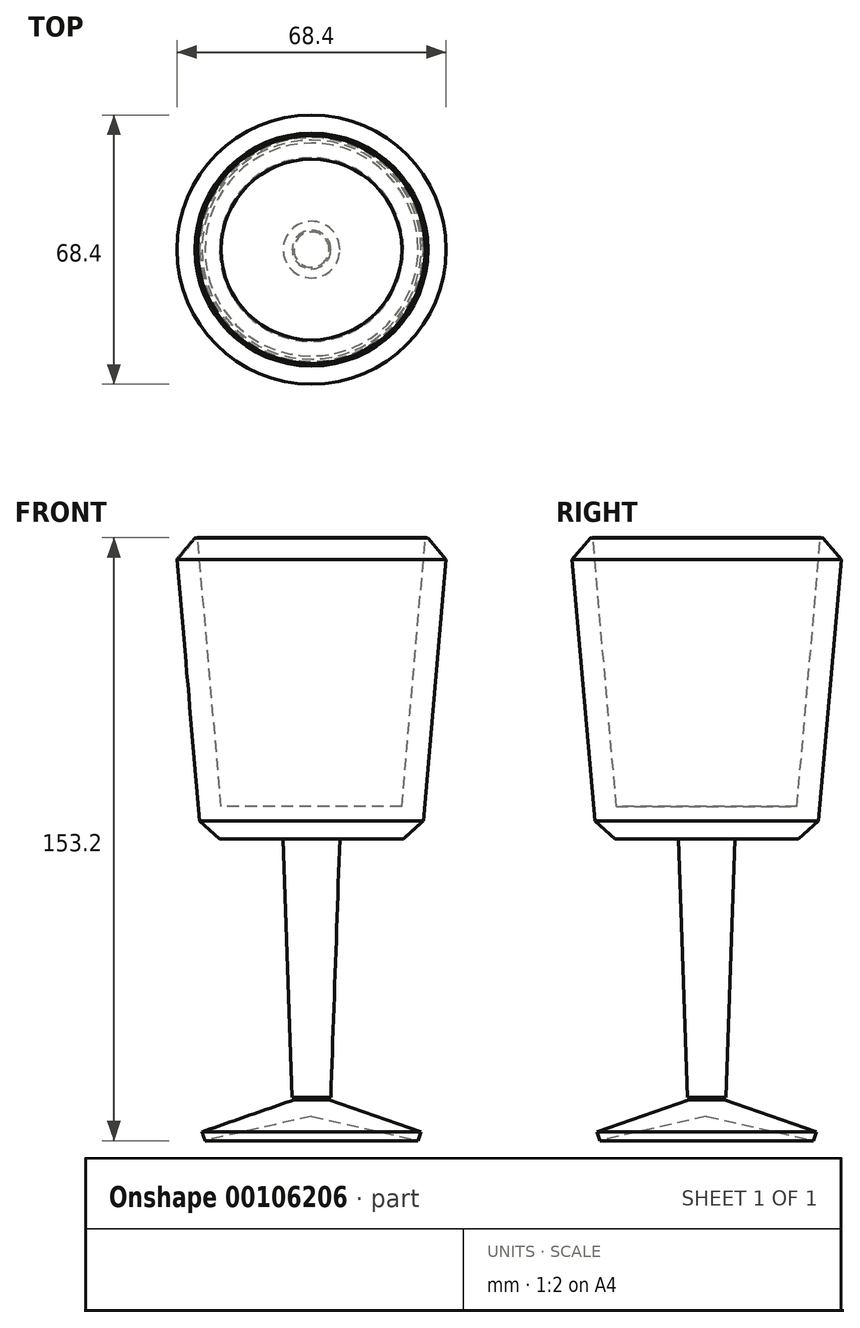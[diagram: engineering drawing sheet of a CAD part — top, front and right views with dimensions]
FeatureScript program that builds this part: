
annotation { "Feature Type Name" : "Feature", "Feature Type Description" : "" }
export const myFeature = defineFeature(function(context is Context, id is Id, definition is map)
    precondition{}
    {
        {
            var Q0;
            Q0=qCreatedBy(makeId("Front.planeOp"),FACE);
            var sketch = newSketch(context, id + "F0", { "sketchPlane" : qUnion([Q0])});
            skLineSegment(sketch, "E0", {"start": v(0, 0) * mm, "end": v(-27.99, 0) * mm});
            skLineSegment(sketch, "E1", {"start": v(-27.99, 0) * mm, "end": v(-34.65, 76.06) * mm});
            skLineSegment(sketch, "E2", {"start": v(-34.65, 76.06) * mm, "end": v(-28.92, 76.56) * mm});
            skLineSegment(sketch, "E3", {"start": v(-28.92, 76.56) * mm, "end": v(-22.94, 8.31) * mm});
            skLineSegment(sketch, "E4", {"start": v(-22.94, 8.31) * mm, "end": v(0, 8.31) * mm});
            skLineSegment(sketch, "E5", {"start": v(0, 8.31) * mm, "end": v(0, 0) * mm});
            skSolve(sketch);
        }
        {
            var Q0;
            Q0=makeQuery(id+"F0.imprint","IMPRINT",FACE,{"disambiguationData":[TD([[makeQuery(id+"F0.imprint","IMPRINT",EDGE,{"derivedFrom":sQuery(id+"F0.wireOp",EDGE,"E0")}),-1.0]])]});
            var Q1;
            Q1=sQuery(id+"F0.wireOp",EDGE,"E5");
            revolve(context, id + "F1", {"entities" : qUnion([Q0]), "axis" : qUnion([Q1]), "revolveType" : RevolveType.FULL});
        }
        {
            var Q0;
            Q0=makeQuery(id+"F1.opRevolve","SWEPT_FACE",FACE,{"disambiguationData":[OSD([sQuery(id+"F0.wireOp",EDGE,"E1")])]});
            chamfer(context, id + "F2", {"entities" : qUnion([Q0]), "width" : 5.08 * mm, "tangentPropagation" : true});
        }
        {
            var Q0;
            Q0=qCreatedBy(makeId("Right.planeOp"),FACE);
            var sketch = newSketch(context, id + "F3", { "sketchPlane" : qUnion([Q0])});
            skLineSegment(sketch, "E6", {"start": v(-7.2, 0) * mm, "end": v(0, 0) * mm});
            skLineSegment(sketch, "E7", {"start": v(0, 0) * mm, "end": v(0, -65.63) * mm});
            skLineSegment(sketch, "E8", {"start": v(0, -65.63) * mm, "end": v(-4.9, -65.63) * mm});
            skLineSegment(sketch, "E9", {"start": v(-4.9, -65.63) * mm, "end": v(-7.2, 0) * mm});
            skSolve(sketch);
        }
        {
            var Q0;
            Q0=makeQuery(id+"F3.imprint","IMPRINT",FACE,{"disambiguationData":[TD([[makeQuery(id+"F3.imprint","IMPRINT",EDGE,{"derivedFrom":sQuery(id+"F3.wireOp",EDGE,"E6")}),-1.0]])]});
            var Q1;
            Q1=sQuery(id+"F3.wireOp",EDGE,"E7");
            revolve(context, id + "F4", {"operationType" : NewBodyOperationType.ADD, "entities" : qUnion([Q0]), "axis" : qUnion([Q1]), "revolveType" : RevolveType.FULL});
        }
        {
            var Q0;
            Q0=qCreatedBy(makeId("Right.planeOp"),FACE);
            var sketch = newSketch(context, id + "F5", { "sketchPlane" : qUnion([Q0])});
            skLineSegment(sketch, "E10", {"start": v(0, -66.25) * mm, "end": v(-4.48, -66.25) * mm});
            skLineSegment(sketch, "E11", {"start": v(-4.48, -66.25) * mm, "end": v(-27.85, -74.39) * mm});
            skLineSegment(sketch, "E12", {"start": v(-27.85, -74.39) * mm, "end": v(-27.06, -76.64) * mm});
            skLineSegment(sketch, "E13", {"start": v(-27.06, -76.64) * mm, "end": v(0, -70.42) * mm});
            skLineSegment(sketch, "E14", {"start": v(0, -70.42) * mm, "end": v(0, -66.25) * mm});
            skSolve(sketch);
        }
        {
            var Q0;
            Q0=makeQuery(id+"F5.imprint","IMPRINT",FACE,{"disambiguationData":[TD([[makeQuery(id+"F5.imprint","IMPRINT",EDGE,{"derivedFrom":sQuery(id+"F5.wireOp",EDGE,"E10")}),1.0]])]});
            var Q1;
            Q1=sQuery(id+"F5.wireOp",EDGE,"E14");
            revolve(context, id + "F6", {"entities" : qUnion([Q0]), "axis" : qUnion([Q1]), "revolveType" : RevolveType.FULL});
        }
    });
